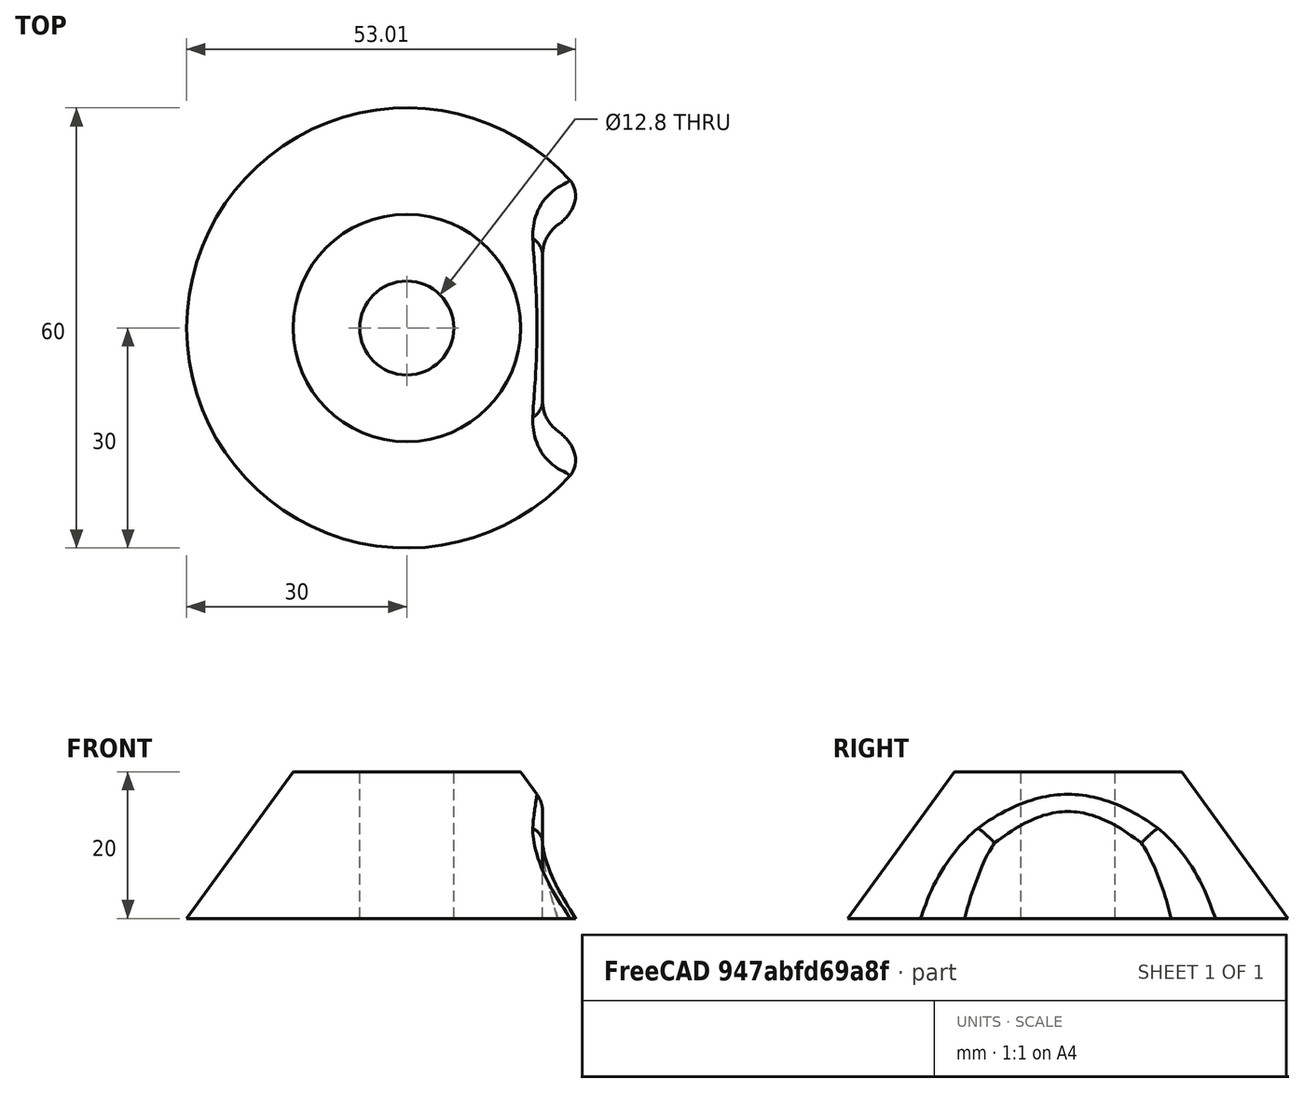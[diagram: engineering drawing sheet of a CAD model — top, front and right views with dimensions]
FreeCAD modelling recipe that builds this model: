
FCSTD DOCUMENT
Label: centercone_v2
objects: Part::Box×2, Part::Fillet×2, Part::MultiFuse×2, Part::Cone×1, Part::Cylinder×1, Part::Cut×1
note: 9 computed .brp shape members not serialized (recipe doc carries the construction recipe); baked Part::Feature solids carry a one-line shape summary decoded from their .brp

FEATURE [Part::Cone] Cone
  Angle = 360
  Height = 40
  Radius1 = 30
  Radius2 = 1
FEATURE [Part::Box] Box
  Height = 40
  Length = 20
  Placement = pos=(18.5,-15,0) rot=(0,0,1;0rad)
  Width = 30
FEATURE [Part::Fillet] Fillet  label="weirdSideThing"
  Base = -> Box
  Edges = 2 edges r=5: [Edge1,Edge3]
FEATURE [Part::Cylinder] Cylinder
  Angle = 360
  Height = 40
  Radius = 6.4
FEATURE [Part::Box] Box001  label="topTrim"
  Height = 40
  Length = 40
  Placement = pos=(-20,-20,20) rot=(0,0,1;0rad)
  Width = 40
FEATURE [Part::MultiFuse] Fusion
  Shapes = -> [Box001,Cylinder]
FEATURE [Part::MultiFuse] Fusion001
  Shapes = -> [Fusion,Fillet]
FEATURE [Part::Cut] Cut
  Base = -> Cone
  Tool = -> Fusion001
FEATURE [Part::Fillet] Fillet001
  Base = -> Cut
  Edges = 4 edges r=4: [Edge2,Edge3,Edge7,Edge8]
